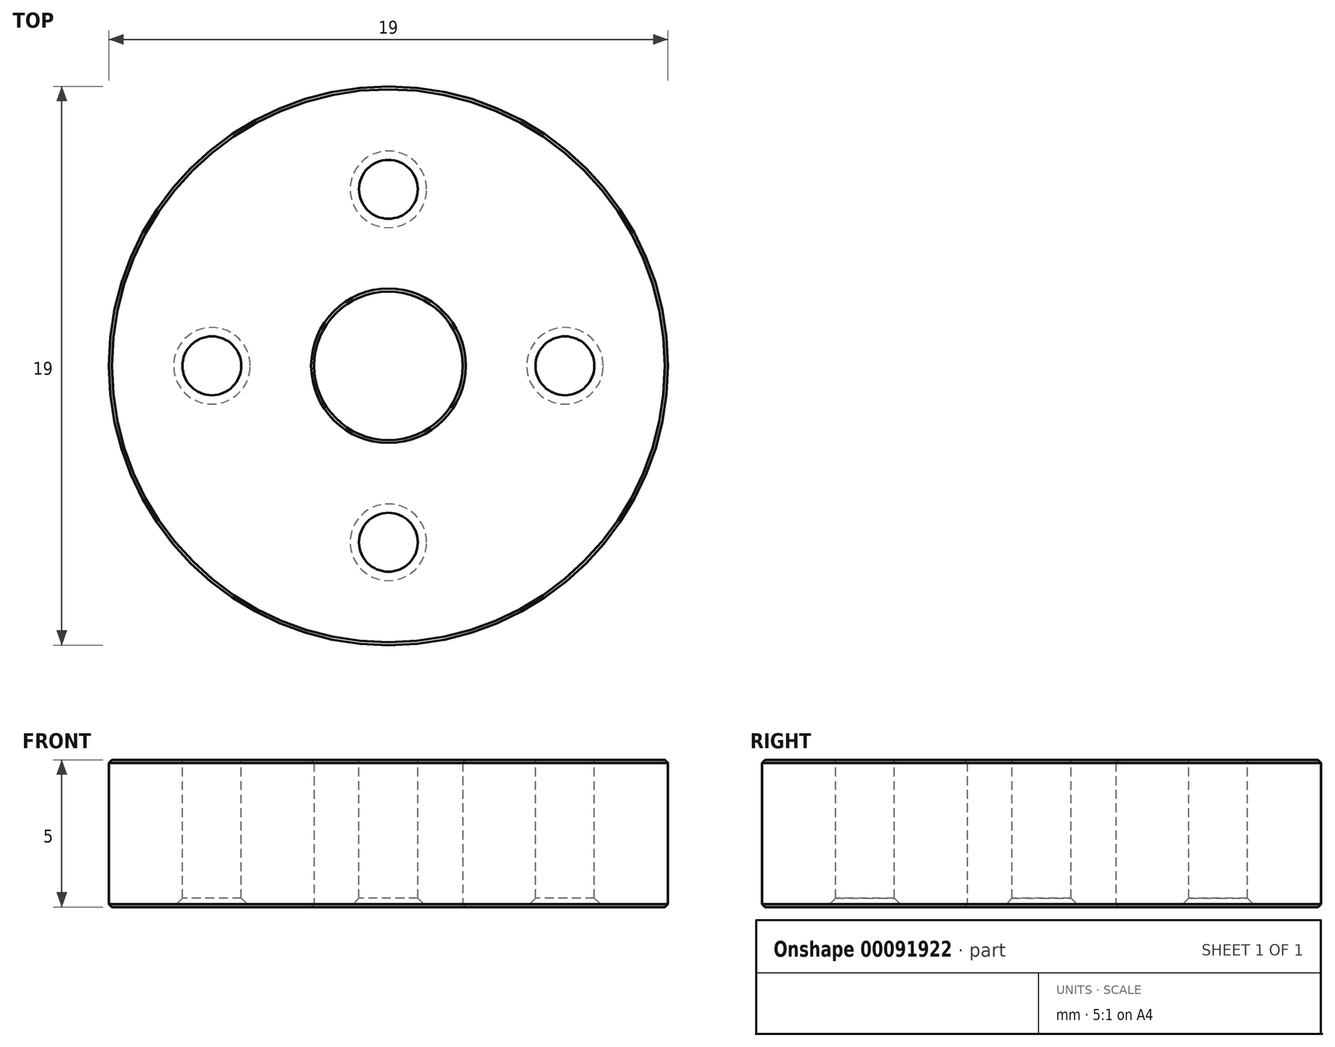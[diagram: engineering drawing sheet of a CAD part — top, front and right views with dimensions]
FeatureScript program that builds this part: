
annotation { "Feature Type Name" : "Feature", "Feature Type Description" : "" }
export const myFeature = defineFeature(function(context is Context, id is Id, definition is map)
    precondition{}
    {
        {
            var Q0;
            Q0=qCreatedBy(makeId("Top.planeOp"),FACE);
            var sketch = newSketch(context, id + "F0", { "sketchPlane" : qUnion([Q0])});
            skCircle(sketch, "E0", {"center": v(0, 0) * mm, "radius": 9.5 * mm});
            skCircle(sketch, "E1", {"center": v(0, 0) * mm, "radius": 2.52 * mm});
            skSolve(sketch);
        }
        {
            var Q0;
            Q0 = qSketchRegion(id + "F0", true);
            extrude(context, id + "F1", {"entities" : qUnion([Q0]), "depth" : 5 * mm});
        }
        {
            var Q0;
            Q0=makeQuery(id+"F1.opExtrude","CAP_EDGE",EDGE,{"disambiguationData":[OSD([sQuery(id+"F0.wireOp",EDGE,"E0")])],"isStart":false});
            var Q1;
            Q1=makeQuery(id+"F1.opExtrude","CAP_EDGE",EDGE,{"disambiguationData":[OSD([sQuery(id+"F0.wireOp",EDGE,"E0")])],"isStart":true});
            var Q2;
            Q2=makeQuery(id+"F1.opExtrude","CAP_EDGE",EDGE,{"disambiguationData":[OSD([sQuery(id+"F0.wireOp",EDGE,"E1")])],"isStart":false});
            var Q3;
            Q3=makeQuery(id+"F1.opExtrude","CAP_EDGE",EDGE,{"disambiguationData":[OSD([sQuery(id+"F0.wireOp",EDGE,"E1")])],"isStart":true});
            chamfer(context, id + "F2", {"entities" : qUnion([Q0, Q1, Q2, Q3]), "width" : .1 * mm, "tangentPropagation" : true});
        }
        {
            var Q0;
            Q0=makeQuery(id+"F1.opExtrude","CAP_FACE",FACE,{"disambiguationData":[OSD([sQuery(id+"F0.wireOp",EDGE,"E0"),sQuery(id+"F0.wireOp",EDGE,"E1")])],"isStart":false});
            var sketch = newSketch(context, id + "F3", { "sketchPlane" : qUnion([Q0])});
            skCircle(sketch, "E2", {"center": v(0, 6) * mm, "radius": 1 * mm});
            skCircle(sketch, "E3.1.0", {"center": v(-6, 0) * mm, "radius": 1 * mm});
            skCircle(sketch, "E3.2.0", {"center": v(0, -6) * mm, "radius": 1 * mm});
            skCircle(sketch, "E3.3.0", {"center": v(6, 0) * mm, "radius": 1 * mm});
            skPoint(sketch, "E3.center", {"position": v(0, 0) * mm});
            skSolve(sketch);
        }
        {
            var Q0;
            Q0 = qSketchRegion(id + "F3", true);
            extrude(context, id + "F4", {"entities" : qUnion([Q0]), "operationType" : NewBodyOperationType.REMOVE, "endBound" : BoundingType.THROUGH_ALL, "oppositeDirection" : true, "depth" : 25 * mm});
        }
        {
            var Q0;
            Q0=makeQuery(id+"F4.boolean.opBoolean","COPY",EDGE,{"derivedFrom":makeQuery(id+"F4.opExtrude","CAP_EDGE",EDGE,{"disambiguationData":[OSD([sQuery(id+"F3.wireOp",EDGE,"E2")])],"isStart":true})});
            var Q1;
            Q1=makeQuery(id+"F4.boolean.opBoolean","COPY",EDGE,{"derivedFrom":makeQuery(id+"F4.opExtrude","CAP_EDGE",EDGE,{"disambiguationData":[OSD([sQuery(id+"F3.wireOp",EDGE,"E3.3.0")])],"isStart":true})});
            var Q2;
            Q2=makeQuery(id+"F4.boolean.opBoolean","COPY",EDGE,{"derivedFrom":makeQuery(id+"F4.opExtrude","CAP_EDGE",EDGE,{"disambiguationData":[OSD([sQuery(id+"F3.wireOp",EDGE,"E3.2.0")])],"isStart":true})});
            var Q3;
            Q3=makeQuery(id+"F4.boolean.opBoolean","COPY",EDGE,{"derivedFrom":makeQuery(id+"F4.opExtrude","CAP_EDGE",EDGE,{"disambiguationData":[OSD([sQuery(id+"F3.wireOp",EDGE,"E3.1.0")])],"isStart":true})});
            var Q4;
            Q4=makeQuery(id+"F4.boolean.opBoolean","INTERSECT",EDGE,{"derivedFrom":[makeQuery(id+"F1.opExtrude","CAP_FACE",FACE,{"disambiguationData":[OSD([sQuery(id+"F0.wireOp",EDGE,"E0"),sQuery(id+"F0.wireOp",EDGE,"E1")])],"isStart":true}),makeQuery(id+"F4.opExtrude","SWEPT_FACE",FACE,{"disambiguationData":[OSD([sQuery(id+"F3.wireOp",EDGE,"E3.1.0")])]})]});
            var Q5;
            Q5=makeQuery(id+"F4.boolean.opBoolean","INTERSECT",EDGE,{"derivedFrom":[makeQuery(id+"F1.opExtrude","CAP_FACE",FACE,{"disambiguationData":[OSD([sQuery(id+"F0.wireOp",EDGE,"E0"),sQuery(id+"F0.wireOp",EDGE,"E1")])],"isStart":true}),makeQuery(id+"F4.opExtrude","SWEPT_FACE",FACE,{"disambiguationData":[OSD([sQuery(id+"F3.wireOp",EDGE,"E2")])]})]});
            var Q6;
            Q6=makeQuery(id+"F4.boolean.opBoolean","INTERSECT",EDGE,{"derivedFrom":[makeQuery(id+"F1.opExtrude","CAP_FACE",FACE,{"disambiguationData":[OSD([sQuery(id+"F0.wireOp",EDGE,"E0"),sQuery(id+"F0.wireOp",EDGE,"E1")])],"isStart":true}),makeQuery(id+"F4.opExtrude","SWEPT_FACE",FACE,{"disambiguationData":[OSD([sQuery(id+"F3.wireOp",EDGE,"E3.3.0")])]})]});
            var Q7;
            Q7=makeQuery(id+"F4.boolean.opBoolean","INTERSECT",EDGE,{"derivedFrom":[makeQuery(id+"F1.opExtrude","CAP_FACE",FACE,{"disambiguationData":[OSD([sQuery(id+"F0.wireOp",EDGE,"E0"),sQuery(id+"F0.wireOp",EDGE,"E1")])],"isStart":true}),makeQuery(id+"F4.opExtrude","SWEPT_FACE",FACE,{"disambiguationData":[OSD([sQuery(id+"F3.wireOp",EDGE,"E3.2.0")])]})]});
            chamfer(context, id + "F5", {"entities" : qUnion([Q0, Q1, Q2, Q3, Q4, Q5, Q6, Q7]), "width" : .3 * mm, "tangentPropagation" : true});
        }
    });
